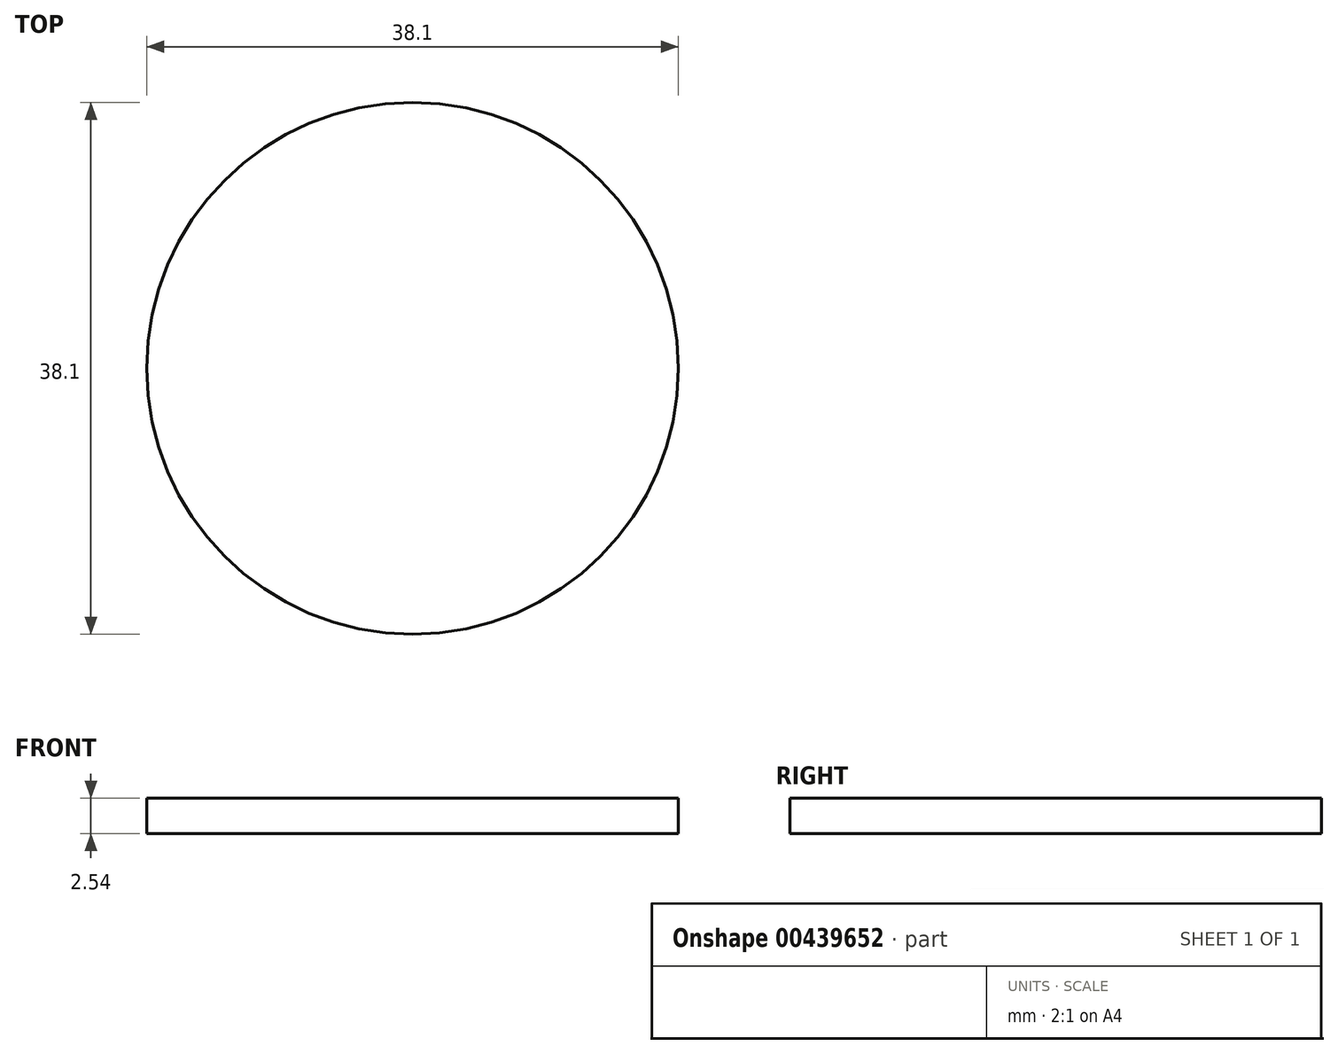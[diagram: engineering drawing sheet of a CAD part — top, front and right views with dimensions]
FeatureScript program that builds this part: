
annotation { "Feature Type Name" : "Feature", "Feature Type Description" : "" }
export const myFeature = defineFeature(function(context is Context, id is Id, definition is map)
    precondition{}
    {
        {
            var Q0;
            Q0=qCreatedBy(makeId("Top.planeOp"),FACE);
            var sketch = newSketch(context, id + "F0", { "sketchPlane" : qUnion([Q0])});
            skCircle(sketch, "E0", {"center": v(0, 0) * mm, "radius": 19.05 * mm});
            skSolve(sketch);
        }
        {
            var Q0;
            Q0 = qSketchRegion(id + "F0", true);
            extrude(context, id + "F1", {"entities" : qUnion([Q0]), "endBound" : BoundingType.SYMMETRIC, "depth" : 2.54 * mm});
        }
    });
